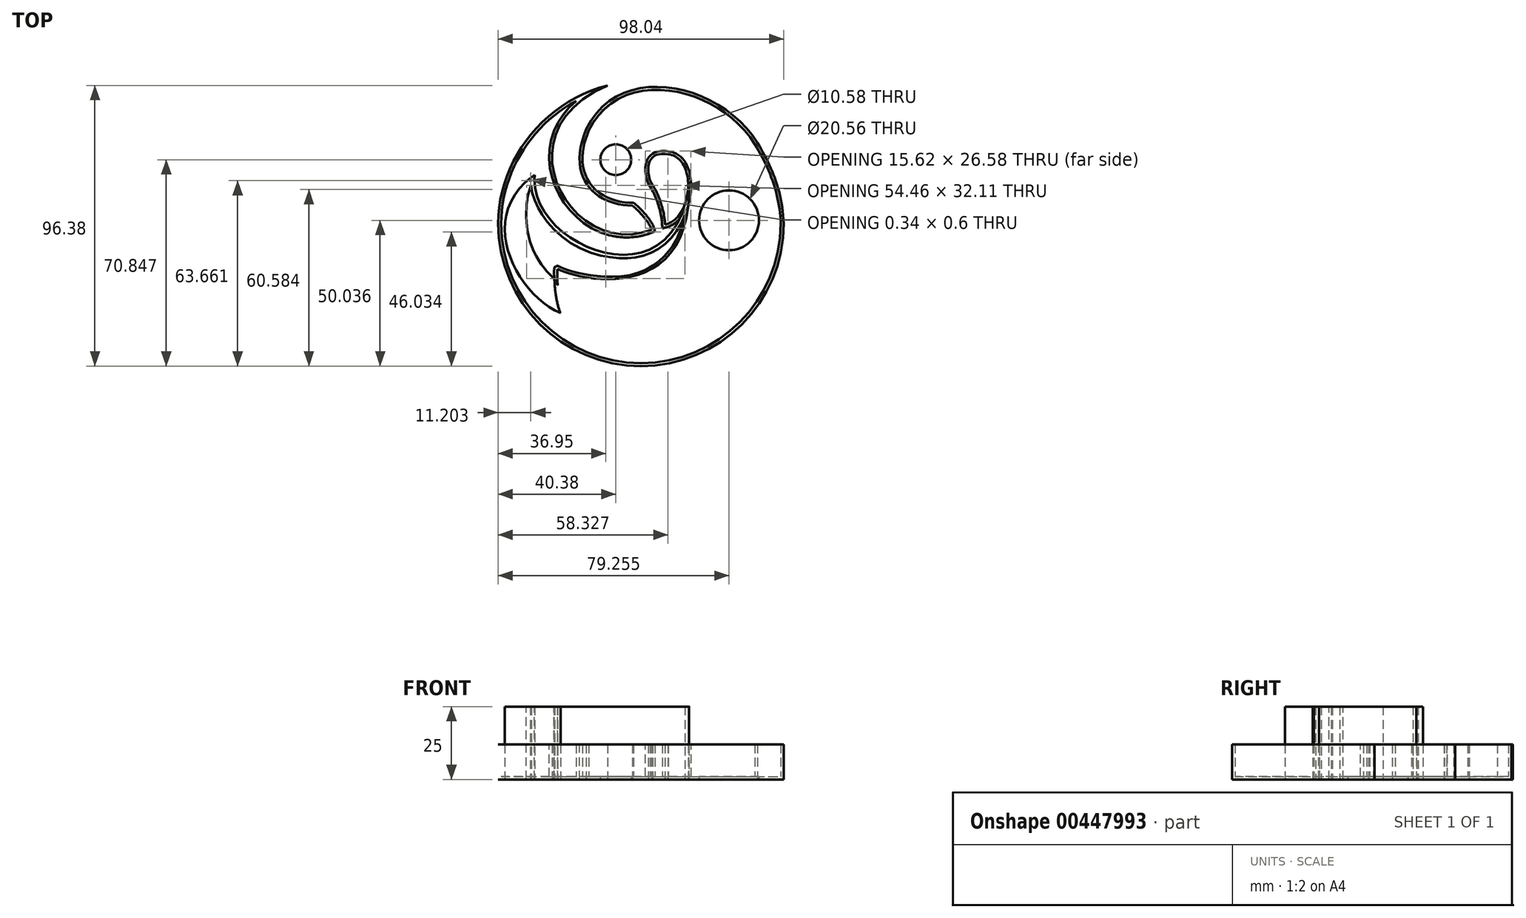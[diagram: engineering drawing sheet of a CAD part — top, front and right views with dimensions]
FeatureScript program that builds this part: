
annotation { "Feature Type Name" : "Feature", "Feature Type Description" : "" }
export const myFeature = defineFeature(function(context is Context, id is Id, definition is map)
    precondition{}
    {
        {
            var Q0;
            Q0=qCreatedBy(makeId("Top.planeOp"),FACE);
            var sketch = newSketch(context, id + "F0", { "sketchPlane" : qUnion([Q0])});
            skArc(sketch, "E0", {"start": v(-47.36, -5.06) * mm, "mid": v(1.66, -54) * mm, "end": v(50.68, -5.06) * mm});
            skFitSpline(sketch, "E1", {"points": [v(5.65, 8.19) * mm, v(10.89, 18.75) * mm], "startDerivative": vector(-5.4, 6.44) * mm, "endDerivative": vector(26.78, -4.12) * mm});
            skFitSpline(sketch, "E2", {"points": [v(10.89, 18.75) * mm, v(9.94, -5.46) * mm], "startDerivative": vector(30.13, -3.1) * mm, "endDerivative": vector(-29.36, -7.21) * mm});
            skFitSpline(sketch, "E3", {"points": [v(5.65, 8.19) * mm, v(9.94, -5.46) * mm], "startDerivative": vector(7.21, -11.59) * mm, "endDerivative": vector(0.77, -13.9) * mm});
            skFitSpline(sketch, "E4", {"points": [v(5.3, -7.18) * mm, v(-1.22, 1.06) * mm], "startDerivative": vector(-2.32, 7.47) * mm, "endDerivative": vector(-7.73, 6.44) * mm});
            skFitSpline(sketch, "E5", {"points": [v(5.3, -7.18) * mm, v(-9.83, 42.37) * mm], "startDerivative": vector(-81.9, -32.48) * mm, "endDerivative": vector(113.4, 47.85) * mm});
            skFitSpline(sketch, "E6", {"points": [v(-9.83, 42.37) * mm, v(-47.36, -5.06) * mm], "startDerivative": vector(-66.8, -17.4) * mm, "endDerivative": vector(-0.3, -64.01) * mm});
            skFitSpline(sketch, "E7", {"points": [v(-1.22, 1.06) * mm, v(-17.13, 27.37) * mm], "startDerivative": vector(-36.97, 0.24) * mm, "endDerivative": vector(21.52, 51.2) * mm});
            skFitSpline(sketch, "E8", {"points": [v(-17.13, 27.37) * mm, v(41.63, 22.67) * mm], "startDerivative": vector(34.5, 70.87) * mm, "endDerivative": vector(37.85, -61.23) * mm});
            skFitSpline(sketch, "E9", {"points": [v(41.63, 22.67) * mm, v(50.68, -5.06) * mm], "startDerivative": vector(14.84, -24.86) * mm, "endDerivative": vector(1.54, -33.83) * mm});
            skSolve(sketch);
        }
        {
            var Q0;
            Q0=makeQuery(id+"F0.imprint","IMPRINT",FACE,{"disambiguationData":[TD([[makeQuery(id+"F0.imprint","IMPRINT",EDGE,{"derivedFrom":sQuery(id+"F0.wireOp",EDGE,"E0")}),1.0]])]});
            extrude(context, id + "F1", {"entities" : qUnion([Q0]), "depth" : 12 * mm});
        }
        {
            var Q0;
            Q0=makeQuery(id+"F1.opExtrude","CAP_FACE",FACE,{"disambiguationData":[OSD([sQuery(id+"F0.wireOp",EDGE,"E0"),sQuery(id+"F0.wireOp",EDGE,"E1"),sQuery(id+"F0.wireOp",EDGE,"E2"),sQuery(id+"F0.wireOp",EDGE,"E3"),sQuery(id+"F0.wireOp",EDGE,"E4"),sQuery(id+"F0.wireOp",EDGE,"E5"),sQuery(id+"F0.wireOp",EDGE,"E6"),sQuery(id+"F0.wireOp",EDGE,"E7"),sQuery(id+"F0.wireOp",EDGE,"E8"),sQuery(id+"F0.wireOp",EDGE,"E9")])],"isStart":false});
            shell(context, id + "F2", {"entities" : qUnion([Q0]), "thickness" : 1 * mm});
        }
        {
            var Q0;
            Q0=qCreatedBy(makeId("Top.planeOp"),FACE);
            var sketch = newSketch(context, id + "F3", { "sketchPlane" : qUnion([Q0])});
            skFitSpline(sketch, "E10", {"points": [v(-34.78, 11.6) * mm, v(18.14, 9.25) * mm], "startDerivative": vector(-9.03, -71.42) * mm, "endDerivative": vector(12.72, 132.17) * mm});
            skFitSpline(sketch, "E11", {"points": [v(-34.78, 11.6) * mm, v(-25.96, -35.8) * mm], "startDerivative": vector(-61.57, -42.28) * mm, "endDerivative": vector(45.97, -19.7) * mm});
            skFitSpline(sketch, "E12", {"points": [v(-34.78, 11.6) * mm, v(-28, -25.32) * mm], "startDerivative": vector(-18.47, -20.53) * mm, "endDerivative": vector(36.55, -30.25) * mm});
            skFitSpline(sketch, "E13", {"points": [v(18.14, 9.25) * mm, v(-28, -19.97) * mm], "startDerivative": vector(4.93, -135.05) * mm, "endDerivative": vector(-10.67, 10.67) * mm});
            skFitSpline(sketch, "E14", {"points": [v(-28, -19.97) * mm, v(-28, -25.32) * mm], "startDerivative": vector(-1.2, -5.91) * mm, "endDerivative": vector(-0.02, -5.26) * mm});
            skFitSpline(sketch, "E15", {"points": [v(-28, -25.32) * mm, v(-25.96, -35.8) * mm], "startDerivative": vector(0.64, -10.06) * mm, "endDerivative": vector(3.89, -9.2) * mm});
            skFitSpline(sketch, "E16", {"points": [v(35.62, -39.5) * mm, v(-25.96, -35.8) * mm], "startDerivative": vector(-59.4, -59.3) * mm, "endDerivative": vector(-21.49, 41.65) * mm});
            skFitSpline(sketch, "E17", {"points": [v(35.62, -39.5) * mm, v(18.14, 23.5) * mm], "startDerivative": vector(57.56, 57.07) * mm, "endDerivative": vector(-86.58, 10.94) * mm});
            skFitSpline(sketch, "E18", {"points": [v(18.14, 23.5) * mm, v(3.84, 14.84) * mm], "startDerivative": vector(-10.02, 0.91) * mm, "endDerivative": vector(-2.28, -18.68) * mm});
            skFitSpline(sketch, "E19", {"points": [v(-28, -19.97) * mm, v(30.06, -16.5) * mm], "startDerivative": vector(6.1, -57.73) * mm, "endDerivative": vector(30.1, 84.76) * mm});
            skFitSpline(sketch, "E20.0", {"points": [v(-28.99, -20.08) * mm, v(-28.85, -21.38) * mm, v(-28.2, -23.87) * mm, v(-26.26, -27.19) * mm, v(-23.5, -30.06) * mm, v(-18.93, -33.27) * mm, v(-11.84, -36.1) * mm, v(-2.05, -37.43) * mm, v(8.12, -36.5) * mm, v(17.77, -33.02) * mm, v(25.94, -26.73) * mm, v(29.7, -20.5) * mm, v(31, -16.84) * mm]});
            skArc(sketch, "E21.0.endCap", {"start": v(17.88, 9.28) * mm, "mid": v(18.17, 9.52) * mm, "end": v(18.4, 9.23) * mm});
            skFitSpline(sketch, "E22.0", {"points": [v(18.05, 22.5) * mm, v(17.89, 22.52) * mm, v(17.49, 22.53) * mm, v(16.46, 22.47) * mm, v(14.86, 22.22) * mm, v(12.67, 21.63) * mm, v(10.42, 20.76) * mm, v(8.3, 19.6) * mm, v(6.54, 18.2) * mm, v(5.3, 16.57) * mm, v(4.9, 15.37) * mm, v(4.83, 14.72) * mm]});
            skFitSpline(sketch, "E23.0", {"points": [v(34.91, -38.79) * mm, v(37.24, -36.48) * mm, v(41.07, -31.23) * mm, v(44.45, -22.02) * mm, v(45.5, -12.17) * mm, v(44.3, -2.35) * mm, v(40.88, 6.75) * mm, v(35.37, 14.44) * mm, v(27.84, 20.08) * mm, v(21.51, 22.07) * mm, v(18.02, 22.5) * mm]});
            skFitSpline(sketch, "E24.0", {"points": [v(34.91, -38.79) * mm, v(32.5, -41.2) * mm, v(27.24, -45.1) * mm, v(18.46, -48.6) * mm, v(9.26, -49.98) * mm, v(0.13, -49.53) * mm, v(-8.42, -47.54) * mm, v(-15.88, -44.3) * mm, v(-21.74, -40.11) * mm, v(-24.24, -36.95) * mm, v(-25.07, -35.34) * mm]});
            skFitSpline(sketch, "E25.0", {"points": [v(-27, -25.25) * mm, v(-26.9, -26.9) * mm, v(-26.53, -30.54) * mm, v(-25.65, -33.97) * mm, v(-25.04, -35.4) * mm]});
            skLineSegment(sketch, "E26", {"start": v(30.06, -16.5) * mm, "end": v(30.94, -17.03) * mm});
            skFitSpline(sketch, "E27", {"points": [v(-26.95, -25.88) * mm, v(-27.87, -24.2) * mm], "startDerivative": vector(-1.14, 1.84) * mm, "endDerivative": vector(-0.83, 2.2) * mm});
            skLineSegment(sketch, "E28", {"start": v(17.94, 22.51) * mm, "end": v(18.19, 22.49) * mm});
            skLineSegment(sketch, "E29", {"start": v(34.91, -38.79) * mm, "end": v(34.91, -38.79) * mm});
            skLineSegment(sketch, "E30", {"start": v(-25.2, -35) * mm, "end": v(-25.06, -35.36) * mm});
            skFitSpline(sketch, "E31.0", {"points": [v(-34.21, 10.78) * mm, v(-36.7, 9.08) * mm, v(-40.58, 5.31) * mm, v(-43.64, -1.03) * mm, v(-44.38, -7.8) * mm, v(-43.13, -14.67) * mm, v(-40.24, -21.25) * mm, v(-36.08, -27.13) * mm, v(-31.05, -31.9) * mm, v(-27.4, -34.1) * mm, v(-25.57, -34.87) * mm]});
            skFitSpline(sketch, "E32.0", {"points": [v(-34.04, 10.94) * mm, v(-34.72, 10.17) * mm, v(-35.94, 8.23) * mm, v(-37.17, 4.29) * mm, v(-37.68, -0.38) * mm, v(-37.32, -7.19) * mm, v(-35.29, -14.3) * mm, v(-31.4, -20.62) * mm, v(-28.82, -23.34) * mm, v(-27.36, -24.55) * mm]});
            skFitSpline(sketch, "E33.0", {"points": [v(-35.77, 11.73) * mm, v(-35.97, 10.15) * mm, v(-35.92, 7) * mm, v(-34.64, 2.44) * mm, v(-32.35, -1.84) * mm, v(-28.18, -7.07) * mm, v(-21.24, -12.5) * mm, v(-13, -15.86) * mm, v(-6.18, -16.93) * mm, v(-1.1, -16.8) * mm, v(3.79, -15.65) * mm, v(8.32, -13.34) * mm, v(12.3, -9.8) * mm, v(15.56, -4.95) * mm, v(17.95, 1.26) * mm, v(18.87, 6.35) * mm, v(19.14, 9.16) * mm]});
            skFitSpline(sketch, "E34.0", {"points": [v(17.14, 9.22) * mm, v(17.35, 3.67) * mm, v(16.59, -3.28) * mm, v(14, -10.2) * mm, v(11.42, -14.35) * mm, v(8.31, -17.56) * mm, v(3.6, -20.76) * mm, v(-3.1, -22.96) * mm, v(-10.09, -23.33) * mm, v(-15.31, -22.9) * mm, v(-18.93, -22.29) * mm, v(-22.1, -21.5) * mm, v(-24.26, -20.79) * mm, v(-25.62, -20.23) * mm, v(-26.44, -19.83) * mm, v(-27.03, -19.49) * mm, v(-27.24, -19.31) * mm, v(-27.29, -19.27) * mm]});
            skLineSegment(sketch, "E35", {"start": v(-28, -19.97) * mm, "end": v(-26.86, -19.58) * mm});
            skFitSpline(sketch, "E36", {"points": [v(7.02, 18.53) * mm, v(4.25, 14.82) * mm], "startDerivative": vector(-2.8, -0.99) * mm, "endDerivative": vector(-1.1, -6.84) * mm});
            skLineSegment(sketch, "E37", {"start": v(3.84, 14.84) * mm, "end": v(4.25, 14.82) * mm});
            skFitSpline(sketch, "E38", {"points": [v(17.03, 2.64) * mm, v(16.33, -2.75) * mm], "startDerivative": vector(-0.7, -5.4) * mm, "endDerivative": vector(-1.1, -5.19) * mm});
            skFitSpline(sketch, "E39", {"points": [v(-28.94, -23.09) * mm, v(-27.87, -24.2) * mm], "startDerivative": vector(0.94, -0.99) * mm, "endDerivative": vector(1.32, -1.26) * mm});
            skFitSpline(sketch, "E40", {"points": [v(-26.95, -25.88) * mm, v(-26.86, -19.58) * mm], "startDerivative": vector(-0.58, 6.5) * mm, "endDerivative": vector(0.74, 6.2) * mm});
            skSolve(sketch);
        }
        {
            var Q0;
            Q0=qCreatedBy(makeId("Top.planeOp"),FACE);
            var sketch = newSketch(context, id + "F4", { "sketchPlane" : qUnion([Q0])});
            skCircle(sketch, "E41", {"center": v(31.9, -3.97) * mm, "radius": 10.28 * mm});
            skCircle(sketch, "E42", {"center": v(-6.98, 16.84) * mm, "radius": 5.29 * mm});
            skSolve(sketch);
        }
        {
            var Q0;
            Q0 = qSketchRegion(id + "F4", true);
            extrude(context, id + "F5", {"entities" : qUnion([Q0]), "operationType" : NewBodyOperationType.REMOVE, "depth" : 25 * mm});
        }
        {
            var Q0;
            Q0 = qSketchRegion(id + "F3", true);
            extrude(context, id + "F6", {"entities" : qUnion([Q0]), "depth" : 25 * mm});
        }
    });
